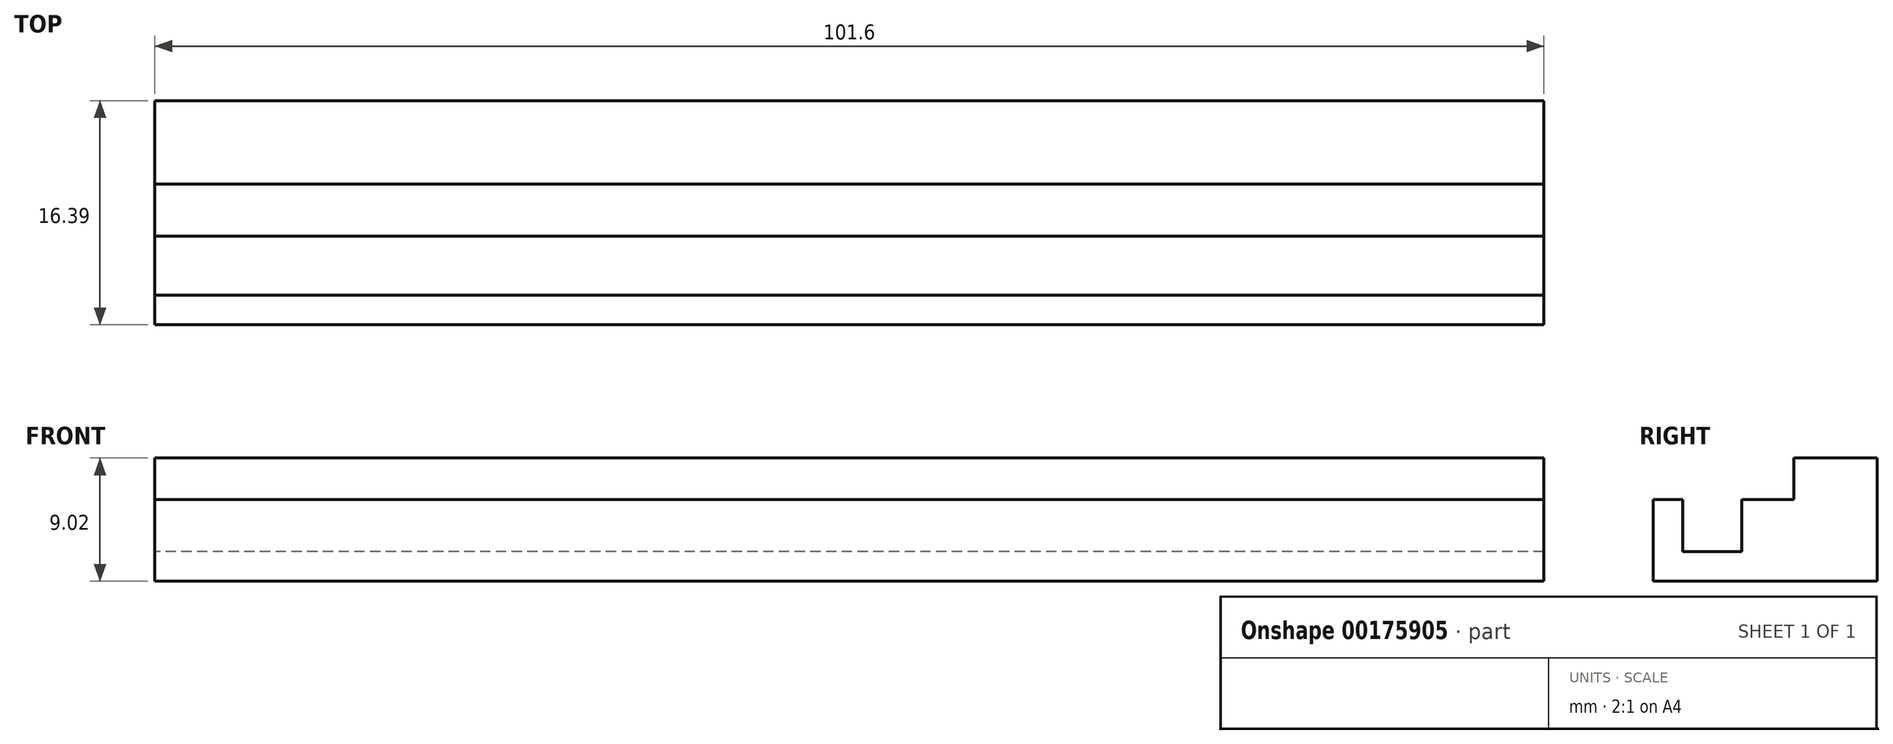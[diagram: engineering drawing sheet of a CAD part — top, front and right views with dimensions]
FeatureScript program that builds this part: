
annotation { "Feature Type Name" : "Feature", "Feature Type Description" : "" }
export const myFeature = defineFeature(function(context is Context, id is Id, definition is map)
    precondition{}
    {
        {
            var Q0;
            Q0=qCreatedBy(makeId("Right.planeOp"),FACE);
            var sketch = newSketch(context, id + "F0", { "sketchPlane" : qUnion([Q0])});
            skLineSegment(sketch, "E0.top", {"start": v(-6.45, -5.97) * mm, "end": v(9.94, -5.97) * mm});
            skLineSegment(sketch, "E0.left", {"start": v(-6.45, 0) * mm, "end": v(-6.45, -5.97) * mm});
            skLineSegment(sketch, "E0.right", {"start": v(9.94, 0) * mm, "end": v(9.94, -5.97) * mm});
            skLineSegment(sketch, "E1", {"start": v(-4.29, 0) * mm, "end": v(-4.29, -3.81) * mm});
            skLineSegment(sketch, "E2", {"start": v(-4.29, -3.81) * mm, "end": v(0.03, -3.81) * mm});
            skLineSegment(sketch, "E3", {"start": v(0.03, -3.81) * mm, "end": v(0.03, 0) * mm});
            skLineSegment(sketch, "E4", {"start": v(-6.45, 0) * mm, "end": v(-4.29, 0) * mm});
            skLineSegment(sketch, "E5", {"start": v(0.03, 0) * mm, "end": v(3.84, 0) * mm});
            skLineSegment(sketch, "E6", {"start": v(9.94, 0) * mm, "end": v(9.94, 3.05) * mm});
            skLineSegment(sketch, "E7", {"start": v(9.94, 3.05) * mm, "end": v(3.84, 3.05) * mm});
            skLineSegment(sketch, "E8", {"start": v(3.84, 3.05) * mm, "end": v(3.84, 0) * mm});
            skSolve(sketch);
        }
        {
            var Q0;
            Q0=makeQuery(id+"F0.imprint","IMPRINT",FACE,{"disambiguationData":[TD([[makeQuery(id+"F0.imprint","IMPRINT",EDGE,{"derivedFrom":sQuery(id+"F0.wireOp",EDGE,"E0.top")}),1.0]])]});
            extrude(context, id + "F1", {"entities" : qUnion([Q0]), "depth" : 101.6 * mm});
        }
    });
